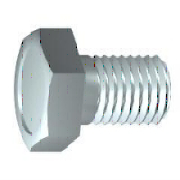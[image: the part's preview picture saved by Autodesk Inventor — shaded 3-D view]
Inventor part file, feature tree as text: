
AUTODESK INVENTOR PART (.ipt)
format: ipt  version: 2023.2 (Build 272271030, 271C)  size: 198,144 bytes
history: native  units: mm
features: sketch x2, revolve x1, thread x1, chamfer x1
ambient origin geometry x8: Origin, YZ Plane, XZ Plane, XY Plane, X Axis, Y Axis, Z Axis, Center Point
bodies: Solid1 (feature_tree)
feature tree (5):
  revolve  "Revolution1"  [1 undecoded]
  thread  "Thread1"  [1 undecoded]
  chamfer  "Chamfer1"  Distance=0.6mm
  sketch  "Sketch1"  dims[d0=24.0mm d1=10.0mm d3=10.0mm]
  sketch  "Sketch2"  dims[d4=14.5mm d5=0.6mm d6=90.0deg d14=8.0mm d15=0.0mm d16=0.833333mm d17=2.0mm d18=45.0deg d23=0.0mm d24=0.0mm d25=0.0mm d26=15.2mm d27=30.0deg d28=12.8mm d29=1.28mm d30=0.3mm d31=6.4mm d32=16.0mm d33=5.8mm d34=0.0mm]
note: 2 required parameter values undecoded (feature->parameter linkage not recoverable at this tier; creation-order binding heuristic only, values carry confidence <= 0.55)